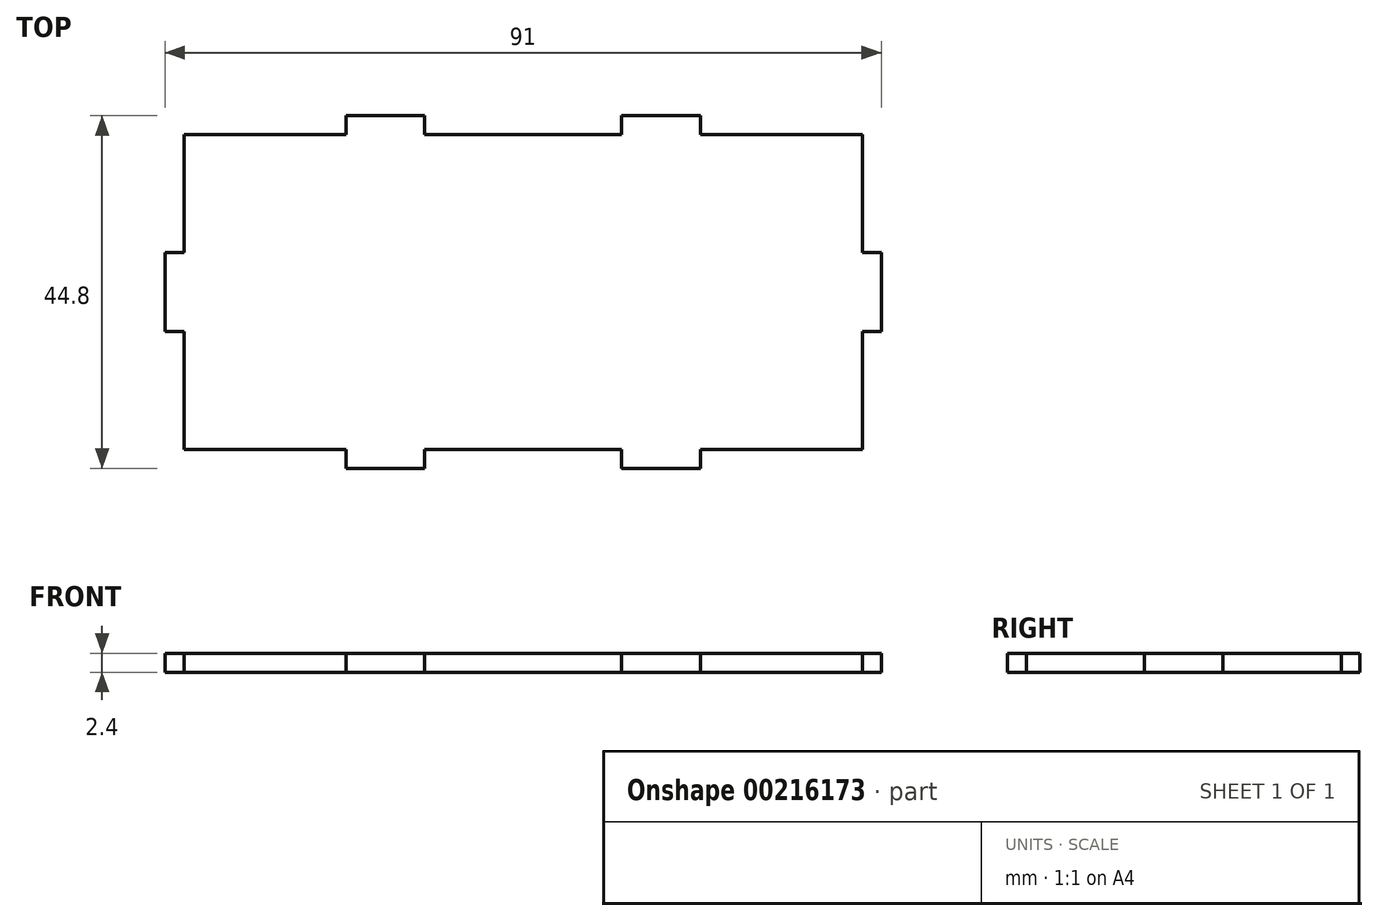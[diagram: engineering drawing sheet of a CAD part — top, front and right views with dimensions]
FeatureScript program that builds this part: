
annotation { "Feature Type Name" : "Feature", "Feature Type Description" : "" }
export const myFeature = defineFeature(function(context is Context, id is Id, definition is map)
    precondition{}
    {
        {
            var Q0;
            Q0=qCreatedBy(makeId("Top.planeOp"),FACE);
            var sketch = newSketch(context, id + "F0", { "sketchPlane" : qUnion([Q0])});
            skLineSegment(sketch, "E0.bottom", {"start": v(43.1, 20) * mm, "end": v(22.5, 20) * mm});
            skLineSegment(sketch, "E0.top", {"start": v(43.1, -20) * mm, "end": v(22.5, -20) * mm});
            skLineSegment(sketch, "E0.left", {"start": v(43.1, 20) * mm, "end": v(43.1, 5) * mm});
            skLineSegment(sketch, "E0.right", {"start": v(-43.1, 20) * mm, "end": v(-43.1, 5) * mm});
            skPoint(sketch, "E0.middle", {"position": v(0, 0) * mm});
            skLineSegment(sketch, "E1.bottom", {"start": v(-12.5, 22.4) * mm, "end": v(-22.5, 22.4) * mm});
            skLineSegment(sketch, "E1.left", {"start": v(-12.5, 22.4) * mm, "end": v(-12.5, 20) * mm});
            skLineSegment(sketch, "E1.right", {"start": v(-22.5, 22.4) * mm, "end": v(-22.5, 20) * mm});
            skPoint(sketch, "E1.middle", {"position": v(-17.5, 20) * mm});
            skLineSegment(sketch, "E2.bottom", {"start": v(22.5, 22.4) * mm, "end": v(12.5, 22.4) * mm});
            skLineSegment(sketch, "E2.left", {"start": v(22.5, 22.4) * mm, "end": v(22.5, 20) * mm});
            skLineSegment(sketch, "E2.right", {"start": v(12.5, 22.4) * mm, "end": v(12.5, 20) * mm});
            skPoint(sketch, "E2.middle", {"position": v(17.5, 20) * mm});
            skLineSegment(sketch, "E3.bottom", {"start": v(45.5, 5) * mm, "end": v(43.1, 5) * mm});
            skLineSegment(sketch, "E3.top", {"start": v(45.5, -5) * mm, "end": v(43.1, -5) * mm});
            skLineSegment(sketch, "E3.left", {"start": v(45.5, 5) * mm, "end": v(45.5, -5) * mm});
            skPoint(sketch, "E3.middle", {"position": v(43.1, 0) * mm});
            skLineSegment(sketch, "E4.top", {"start": v(22.5, -22.4) * mm, "end": v(12.5, -22.4) * mm});
            skLineSegment(sketch, "E4.left", {"start": v(22.5, -20) * mm, "end": v(22.5, -22.4) * mm});
            skLineSegment(sketch, "E4.right", {"start": v(12.5, -20) * mm, "end": v(12.5, -22.4) * mm});
            skPoint(sketch, "E4.middle", {"position": v(17.5, -20) * mm});
            skLineSegment(sketch, "E5.top", {"start": v(-12.5, -22.4) * mm, "end": v(-22.5, -22.4) * mm});
            skLineSegment(sketch, "E5.left", {"start": v(-12.5, -20) * mm, "end": v(-12.5, -22.4) * mm});
            skLineSegment(sketch, "E5.right", {"start": v(-22.5, -20) * mm, "end": v(-22.5, -22.4) * mm});
            skPoint(sketch, "E5.middle", {"position": v(-17.5, -20) * mm});
            skLineSegment(sketch, "E6.bottom", {"start": v(-45.5, 5) * mm, "end": v(-43.1, 5) * mm});
            skLineSegment(sketch, "E6.top", {"start": v(-45.5, -5) * mm, "end": v(-43.1, -5) * mm});
            skLineSegment(sketch, "E6.left", {"start": v(-45.5, 5) * mm, "end": v(-45.5, -5) * mm});
            skPoint(sketch, "E6.middle", {"position": v(-43.1, 0) * mm});
            skLineSegment(sketch, "E7.trimOffspring", {"start": v(-22.5, 20) * mm, "end": v(-43.1, 20) * mm});
            skLineSegment(sketch, "E8.trimOffspring", {"start": v(43.1, -5) * mm, "end": v(43.1, -20) * mm});
            skLineSegment(sketch, "E9.trimOffspring", {"start": v(12.5, -20) * mm, "end": v(-12.5, -20) * mm});
            skLineSegment(sketch, "E10.trimOffspring", {"start": v(-22.5, -20) * mm, "end": v(-43.1, -20) * mm});
            skLineSegment(sketch, "E11.trimOffspring", {"start": v(-43.1, -5) * mm, "end": v(-43.1, -20) * mm});
            skLineSegment(sketch, "E12", {"start": v(-12.5, 20) * mm, "end": v(12.5, 20) * mm});
            skSolve(sketch);
        }
        {
            var Q0;
            Q0=makeQuery(id+"F0.imprint","IMPRINT",FACE,{"disambiguationData":[TD([[makeQuery(id+"F0.imprint","IMPRINT",EDGE,{"derivedFrom":sQuery(id+"F0.wireOp",EDGE,"E0.bottom")}),1.0]])]});
            extrude(context, id + "F1", {"entities" : qUnion([Q0]), "depth" : 2.4 * mm});
        }
    });
